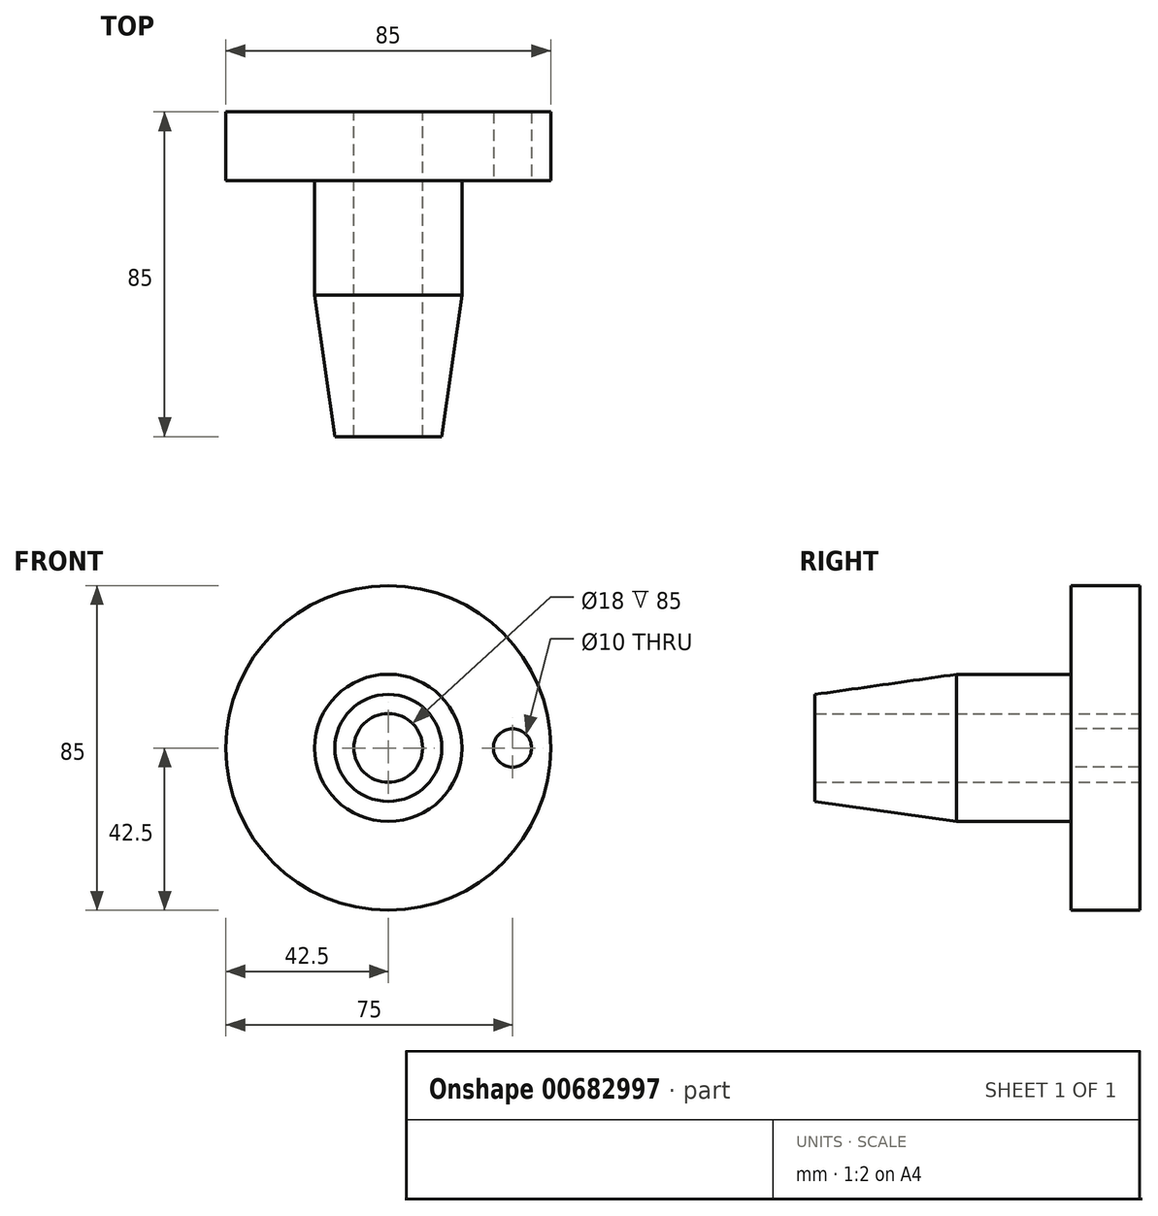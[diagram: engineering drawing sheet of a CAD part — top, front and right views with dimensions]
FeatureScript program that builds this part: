
annotation { "Feature Type Name" : "Feature", "Feature Type Description" : "" }
export const myFeature = defineFeature(function(context is Context, id is Id, definition is map)
    precondition{}
    {
        {
            var Q0;
            Q0=qCreatedBy(makeId("Top.planeOp"),FACE);
            var sketch = newSketch(context, id + "F0", { "sketchPlane" : qUnion([Q0])});
            skLineSegment(sketch, "E0", {"start": v(9, 60.94) * mm, "end": v(9, -24.06) * mm});
            skLineSegment(sketch, "E1", {"start": v(9, -24.06) * mm, "end": v(14, -24.06) * mm});
            skLineSegment(sketch, "E2", {"start": v(14, -24.06) * mm, "end": v(19.28, 12.94) * mm});
            skLineSegment(sketch, "E3", {"start": v(19.28, 12.94) * mm, "end": v(19.28, 42.94) * mm});
            skLineSegment(sketch, "E4", {"start": v(19.28, 42.94) * mm, "end": v(42.5, 42.94) * mm});
            skLineSegment(sketch, "E5", {"start": v(42.5, 42.94) * mm, "end": v(42.5, 60.94) * mm});
            skLineSegment(sketch, "E6", {"start": v(42.5, 60.94) * mm, "end": v(9, 60.94) * mm});
            skLineSegment(sketch, "E7", {"start": v(0, 61.13) * mm, "end": v(0, -25.38) * mm, "construction": true});
            skSolve(sketch);
        }
        {
            var Q0;
            Q0 = qSketchRegion(id + "F0", true);
            var Q1;
            Q1=sQuery(id+"F0.wireOp",EDGE,"E7");
            revolve(context, id + "F1", {"entities" : qUnion([Q0]), "axis" : qUnion([Q1]), "revolveType" : RevolveType.FULL});
        }
        {
            var Q0;
            Q0=makeQuery(id+"F1.opRevolve","SWEPT_FACE",FACE,{"disambiguationData":[OSD([sQuery(id+"F0.wireOp",EDGE,"E4")])]});
            var sketch = newSketch(context, id + "F2", { "sketchPlane" : qUnion([Q0])});
            skCircle(sketch, "E8", {"center": v(32.5, 0) * mm, "radius": 5 * mm});
            skSolve(sketch);
        }
        {
            var Q0;
            Q0=sQuery(id+"F2.wireOp",VERTEX,"E8.center");
            var Q1;
            Q1=makeQuery(id+"F1.opRevolve","SWEPT_BODY",BODY,{"disambiguationData":[OSD([sQuery(id+"F0.wireOp",EDGE,"E0"),sQuery(id+"F0.wireOp",EDGE,"E1"),sQuery(id+"F0.wireOp",EDGE,"E2"),sQuery(id+"F0.wireOp",EDGE,"E3"),sQuery(id+"F0.wireOp",EDGE,"E4"),sQuery(id+"F0.wireOp",EDGE,"E5"),sQuery(id+"F0.wireOp",EDGE,"E6")])]});
            hole(context, id + "F3", {"style" : HoleStyle.SIMPLE, "endStyle" : HoleEndStyle.THROUGH, "holeDiameter" : 10 * mm, "majorDiameter" : 6.35 * mm, "isTappedThrough" : true, "tappedDepth" : 12.7 * mm, "tapClearance" : 3, "locations" : qUnion([Q0]), "scope" : qUnion([Q1])});
        }
    });
